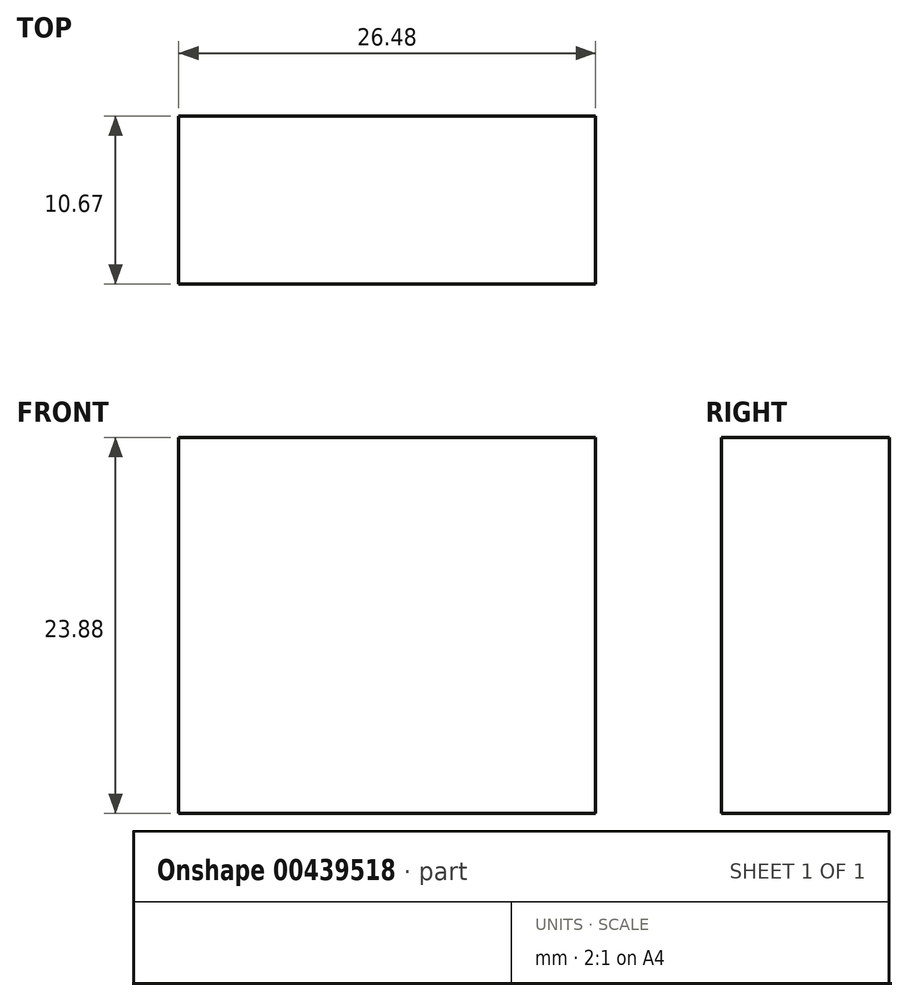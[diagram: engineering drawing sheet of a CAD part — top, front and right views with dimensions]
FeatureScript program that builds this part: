
annotation { "Feature Type Name" : "Feature", "Feature Type Description" : "" }
export const myFeature = defineFeature(function(context is Context, id is Id, definition is map)
    precondition{}
    {
        {
            var Q0;
            Q0=qCreatedBy(makeId("Front.planeOp"),FACE);
            var sketch = newSketch(context, id + "F0", { "sketchPlane" : qUnion([Q0])});
            skLineSegment(sketch, "E0.bottom", {"start": v(-21, 27.05) * mm, "end": v(5.47, 27.05) * mm});
            skLineSegment(sketch, "E0.top", {"start": v(-21, 3.17) * mm, "end": v(5.47, 3.17) * mm});
            skLineSegment(sketch, "E0.left", {"start": v(-21, 27.05) * mm, "end": v(-21, 3.17) * mm});
            skLineSegment(sketch, "E0.right", {"start": v(5.47, 27.05) * mm, "end": v(5.47, 3.17) * mm});
            skSolve(sketch);
        }
        {
            var Q0;
            Q0 = qSketchRegion(id + "F0", true);
            extrude(context, id + "F1", {"entities" : qUnion([Q0]), "depth" : 10.67 * mm});
        }
    });
